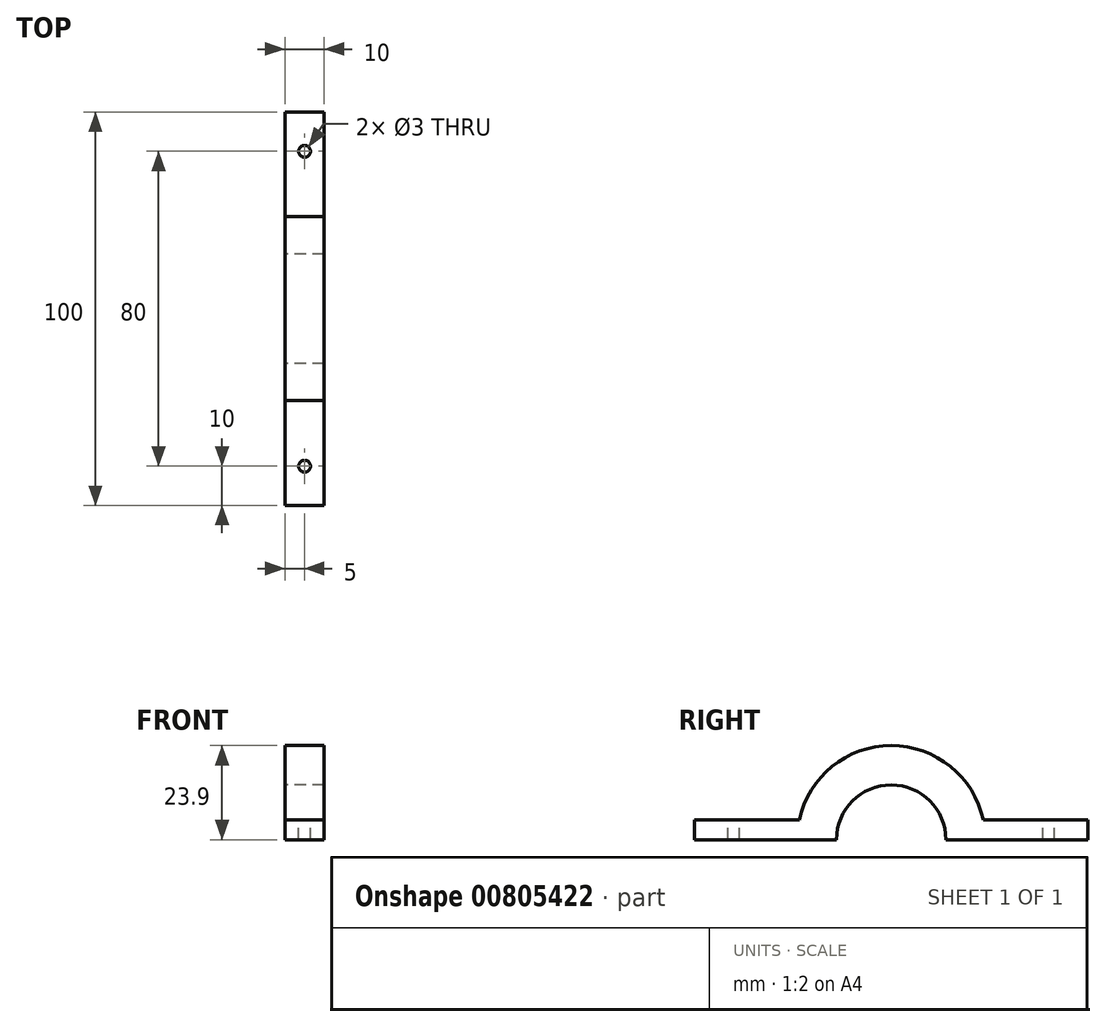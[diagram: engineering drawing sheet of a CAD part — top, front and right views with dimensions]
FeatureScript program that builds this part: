
annotation { "Feature Type Name" : "Feature", "Feature Type Description" : "" }
export const myFeature = defineFeature(function(context is Context, id is Id, definition is map)
    precondition{}
    {
        {
            var Q0;
            Q0=qCreatedBy(makeId("Right.planeOp"),FACE);
            var sketch = newSketch(context, id + "F0", { "sketchPlane" : qUnion([Q0])});
            skArc(sketch, "E0", {"start": v(0, 13.9) * mm, "mid": v(9.83, 9.83) * mm, "end": v(13.9, 0) * mm});
            skArc(sketch, "E1", {"start": v(0, 23.9) * mm, "mid": v(15.03, 18.58) * mm, "end": v(23.37, 5) * mm});
            skLineSegment(sketch, "E2.bottom", {"start": v(13.9, 0) * mm, "end": v(50, 0) * mm});
            skLineSegment(sketch, "E2.top", {"start": v(23.37, 5) * mm, "end": v(50, 5) * mm});
            skLineSegment(sketch, "E2.right", {"start": v(50, 0) * mm, "end": v(50, 5) * mm});
            skPoint(sketch, "E3.orphan", {"position": v(23.9, 0) * mm});
            skArc(sketch, "E4.MirrorCS", {"start": v(0, 23.9) * mm, "mid": v(-15.03, 18.58) * mm, "end": v(-23.37, 5) * mm});
            skLineSegment(sketch, "E5.MirrorCS", {"start": v(-13.9, 0) * mm, "end": v(-50, 0) * mm});
            skArc(sketch, "E6.MirrorCS", {"start": v(0, 13.9) * mm, "mid": v(-9.83, 9.83) * mm, "end": v(-13.9, 0) * mm});
            skLineSegment(sketch, "E7.MirrorCS", {"start": v(-23.37, 5) * mm, "end": v(-50, 5) * mm});
            skLineSegment(sketch, "E8.MirrorCS", {"start": v(-50, 0) * mm, "end": v(-50, 5) * mm});
            skPoint(sketch, "E9.MirrorP", {"position": v(-23.9, 0) * mm});
            skSolve(sketch);
        }
        {
            var Q0;
            Q0 = qSketchRegion(id + "F0", true);
            extrude(context, id + "F1", {"entities" : qUnion([Q0]), "depth" : 10 * mm, "offsetDistance" : 25 * mm});
        }
        {
            var Q0;
            Q0=makeQuery(id+"F1.opExtrude","SWEPT_FACE",FACE,{"disambiguationData":[OSD([sQuery(id+"F0.wireOp",EDGE,"E2.top")])]});
            var sketch = newSketch(context, id + "F2", { "sketchPlane" : qUnion([Q0])});
            skPoint(sketch, "E10.0", {"position": v(5, 50) * mm});
            skPoint(sketch, "E11.0", {"position": v(5, -50) * mm});
            skLineSegment(sketch, "E12", {"start": v(5, 50) * mm, "end": v(5, -50) * mm, "construction": true});
            skCircle(sketch, "E13", {"center": v(5, 40) * mm, "radius": 1.5 * mm});
            skCircle(sketch, "E14.MirrorC", {"center": v(5, -40) * mm, "radius": 1.5 * mm});
            skSolve(sketch);
        }
        {
            var Q0;
            Q0 = qSketchRegion(id + "F2", true);
            extrude(context, id + "F3", {"entities" : qUnion([Q0]), "operationType" : NewBodyOperationType.REMOVE, "oppositeDirection" : true, "depth" : 25 * mm, "offsetDistance" : 25 * mm});
        }
    });
